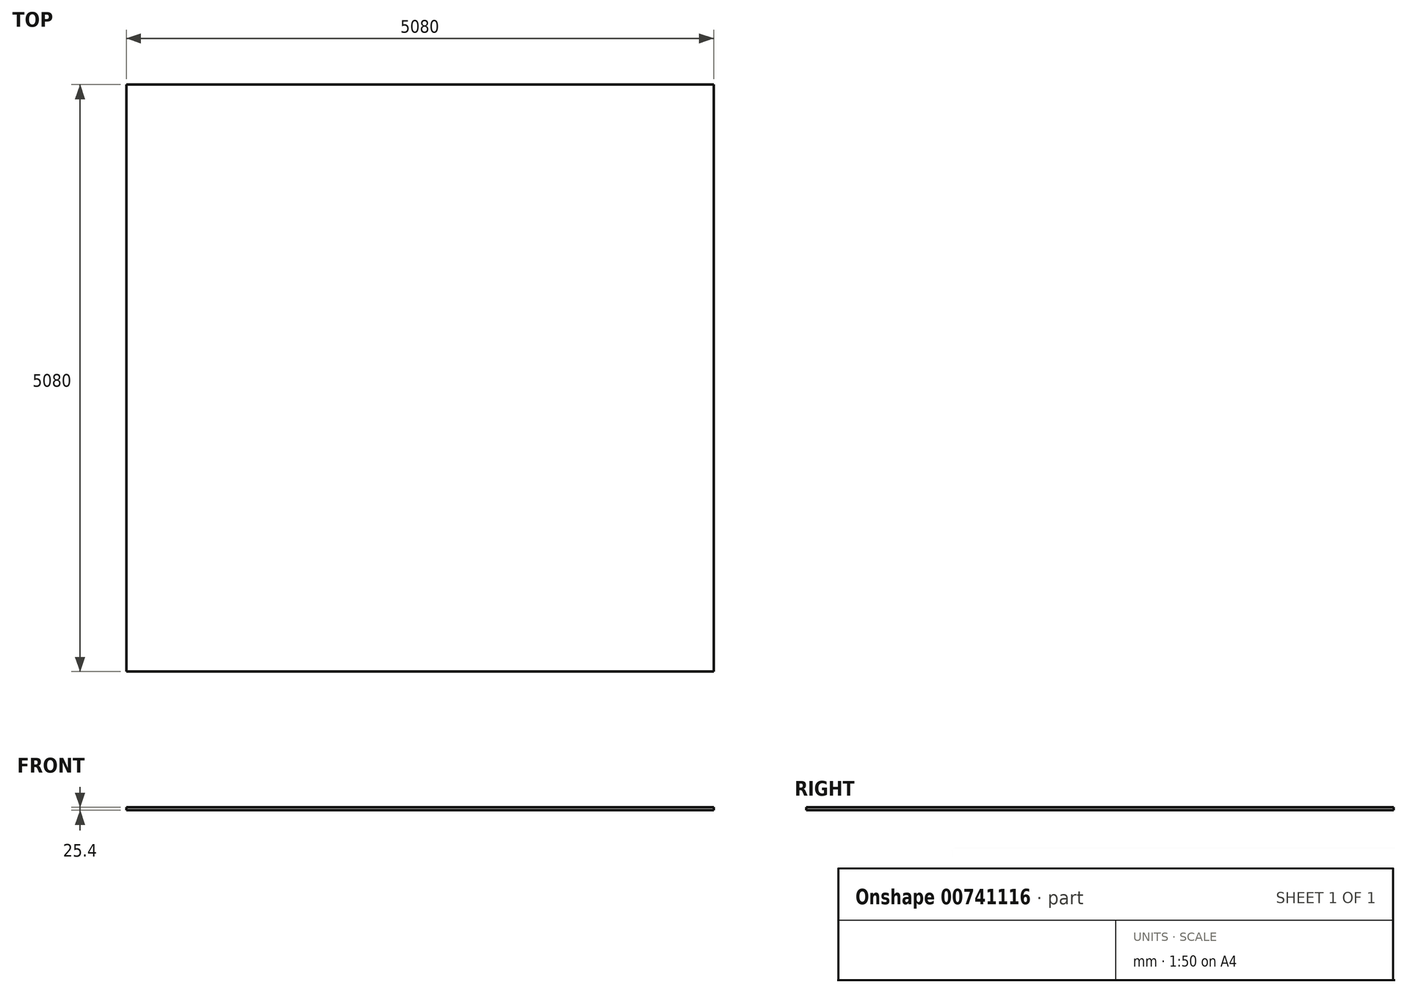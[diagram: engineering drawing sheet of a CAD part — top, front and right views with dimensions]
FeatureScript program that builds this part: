
annotation { "Feature Type Name" : "Feature", "Feature Type Description" : "" }
export const myFeature = defineFeature(function(context is Context, id is Id, definition is map)
    precondition{}
    {
        {
            var Q0;
            Q0=qCreatedBy(makeId("Top.planeOp"),FACE);
            var sketch = newSketch(context, id + "F0", { "sketchPlane" : qUnion([Q0])});
            skLineSegment(sketch, "E0.bottom", {"start": v(1270, -1270) * mm, "end": v(6350, -1270) * mm});
            skLineSegment(sketch, "E0.top", {"start": v(1270, -6350) * mm, "end": v(6350, -6350) * mm});
            skLineSegment(sketch, "E0.left", {"start": v(1270, -1270) * mm, "end": v(1270, -6350) * mm});
            skLineSegment(sketch, "E0.right", {"start": v(6350, -1270) * mm, "end": v(6350, -6350) * mm});
            skSolve(sketch);
        }
        {
            var Q0;
            Q0=makeQuery(id+"F0.imprint","IMPRINT",FACE,{"disambiguationData":[TD([[makeQuery(id+"F0.imprint","IMPRINT",EDGE,{"derivedFrom":sQuery(id+"F0.wireOp",EDGE,"E0.bottom")}),-1.0]])]});
            extrude(context, id + "F1", {"entities" : qUnion([Q0]), "depth" : 25.4 * mm, "offsetDistance" : 25.4 * mm});
        }
    });
